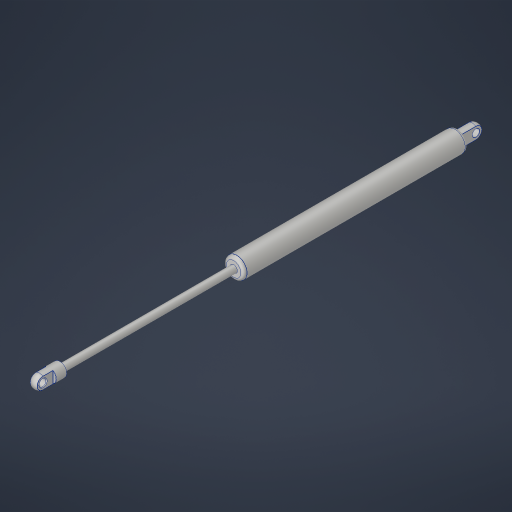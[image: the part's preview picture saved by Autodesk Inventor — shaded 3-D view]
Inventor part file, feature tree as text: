
AUTODESK INVENTOR PART (.ipt)
format: ipt  version: 2023.4 (Build 274418000, 418)  size: 314,880 bytes
history: native  units: in
note: dims shown in document units (in); Inventor stores cm internally (conversion verified against a paired STEP export)
features: fillet x2, other x2
ambient origin geometry x8: Origin, YZ Plane, XZ Plane, XY Plane, X Axis, Y Axis, Z Axis, Center Point
bodies: Solid1 (feature_tree), Solid2 (feature_tree), Solid3 (feature_tree), Solid4 (feature_tree)
feature tree (4):
  fillet  "Fillet5"  [1 undecoded]
  fillet  "Fillet6"  [1 undecoded]
  other  "Boss-Extrude1"
  other  "Cut-Extrude-Thin1"
note: 2 required parameter values undecoded (feature->parameter linkage not recoverable at this tier; creation-order binding heuristic only, values carry confidence <= 0.55)
